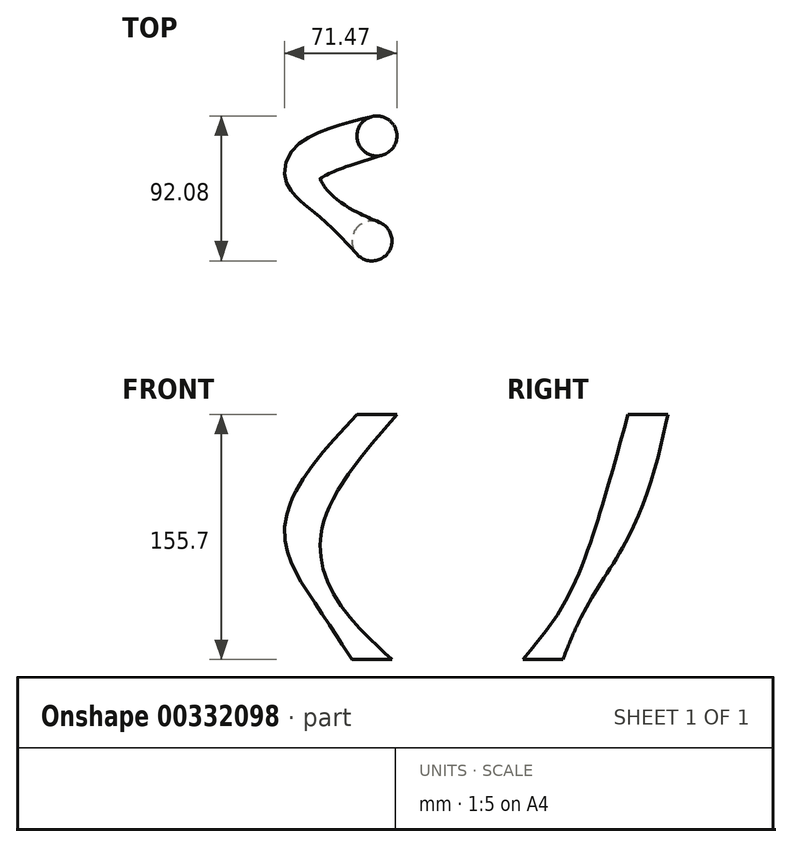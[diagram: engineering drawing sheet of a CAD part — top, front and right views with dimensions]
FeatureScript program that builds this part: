
annotation { "Feature Type Name" : "Feature", "Feature Type Description" : "" }
export const myFeature = defineFeature(function(context is Context, id is Id, definition is map)
    precondition{}
    {
        {
            var Q0;
            Q0=qCreatedBy(makeId("Top.planeOp"),FACE);
            cPlane(context, id + "F0", {"entities" : qUnion([Q0]), "cplaneType" : CPlaneType.OFFSET, "offset" : 78.23 * mm, "width" : 152.4 * mm, "height" : 152.4 * mm});
        }
        {
            var Q0;
            Q0=qCreatedBy(makeId("Top.planeOp"),FACE);
            cPlane(context, id + "F1", {"entities" : qUnion([Q0]), "cplaneType" : CPlaneType.OFFSET, "offset" : 77.47 * mm, "oppositeDirection" : true, "width" : 152.4 * mm, "height" : 152.4 * mm});
        }
        {
            var Q0;
            Q0=qCreatedBy(id+"F1.planeOp",FACE);
            var sketch = newSketch(context, id + "F2", { "sketchPlane" : qUnion([Q0])});
            skCircle(sketch, "E0", {"center": v(44.07, -42.69) * mm, "radius": 12.7 * mm});
            skSolve(sketch);
        }
        {
            var Q0;
            Q0=qCreatedBy(makeId("Top.planeOp"),FACE);
            var sketch = newSketch(context, id + "F3", { "sketchPlane" : qUnion([Q0])});
            skCircle(sketch, "E1", {"center": v(0, 0) * mm, "radius": 11.43 * mm});
            skSolve(sketch);
        }
        {
            var Q0;
            Q0=qCreatedBy(id+"F0.planeOp",FACE);
            var sketch = newSketch(context, id + "F4", { "sketchPlane" : qUnion([Q0])});
            skCircle(sketch, "E2", {"center": v(47.2, 23.99) * mm, "radius": 12.7 * mm});
            skSolve(sketch);
        }
        {
            var Q0;
            Q0=makeQuery(id+"F4.imprint","IMPRINT",FACE,{"disambiguationData":[TD([[makeQuery(id+"F4.imprint","IMPRINT",EDGE,{"derivedFrom":sQuery(id+"F4.wireOp",EDGE,"E2")}),1.0]])]});
            var Q1;
            Q1=makeQuery(id+"F3.imprint","IMPRINT",FACE,{"disambiguationData":[TD([[makeQuery(id+"F3.imprint","IMPRINT",EDGE,{"derivedFrom":sQuery(id+"F3.wireOp",EDGE,"E1")}),1.0]])]});
            var Q2;
            Q2=makeQuery(id+"F2.imprint","IMPRINT",FACE,{"disambiguationData":[TD([[makeQuery(id+"F2.imprint","IMPRINT",EDGE,{"derivedFrom":sQuery(id+"F2.wireOp",EDGE,"E0")}),1.0]])]});
            loft(context, id + "F5", {"sheetProfilesArray" : [{ "sheetProfileEntities" : qUnion([Q0]) }, { "sheetProfileEntities" : qUnion([Q1]) }, { "sheetProfileEntities" : qUnion([Q2]) }]});
        }
    });
